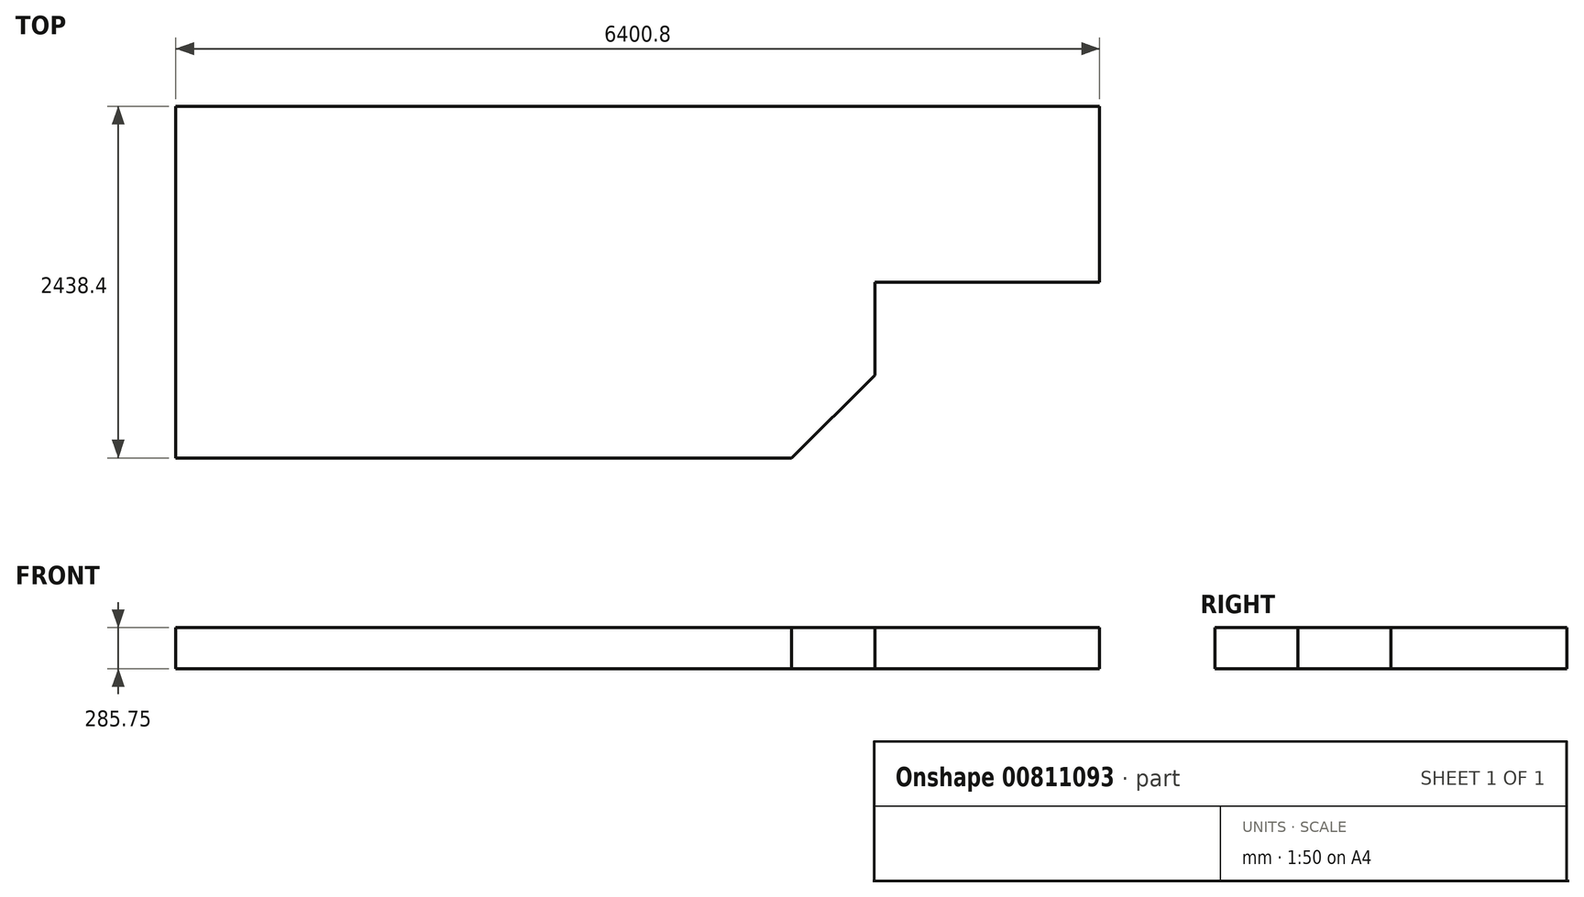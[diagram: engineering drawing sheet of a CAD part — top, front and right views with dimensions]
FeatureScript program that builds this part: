
annotation { "Feature Type Name" : "Feature", "Feature Type Description" : "" }
export const myFeature = defineFeature(function(context is Context, id is Id, definition is map)
    precondition{}
    {
        {
            var Q0;
            Q0=qCreatedBy(makeId("Top.planeOp"),FACE);
            var sketch = newSketch(context, id + "F0", { "sketchPlane" : qUnion([Q0])});
            skLineSegment(sketch, "E0", {"start": v(0, -2438.4) * mm, "end": v(1625.6, -2438.4) * mm});
            skLineSegment(sketch, "E1", {"start": v(4267.2, -2438.4) * mm, "end": v(4841.94, -1863.66) * mm});
            skLineSegment(sketch, "E2", {"start": v(4841.94, -1863.66) * mm, "end": v(4841.94, -1219.2) * mm});
            skLineSegment(sketch, "E3", {"start": v(4841.94, -1219.2) * mm, "end": v(5181.6, -1219.2) * mm});
            skLineSegment(sketch, "E4", {"start": v(5181.6, -1219.2) * mm, "end": v(6400.8, -1219.2) * mm});
            skLineSegment(sketch, "E5", {"start": v(6400.8, -1219.2) * mm, "end": v(6400.8, 0) * mm});
            skLineSegment(sketch, "E6", {"start": v(6400.8, 0) * mm, "end": v(0, 0) * mm});
            skLineSegment(sketch, "E7", {"start": v(1625.6, -2438.4) * mm, "end": v(3251.2, -2438.4) * mm});
            skLineSegment(sketch, "E8", {"start": v(3251.2, -2438.4) * mm, "end": v(4267.2, -2438.4) * mm});
            skLineSegment(sketch, "E9", {"start": v(0, 0) * mm, "end": v(0, -812.8) * mm});
            skLineSegment(sketch, "E10", {"start": v(0, -812.8) * mm, "end": v(0, -2438.4) * mm});
            skSolve(sketch);
        }
        {
            var Q0;
            Q0=makeQuery(id+"F0.imprint","IMPRINT",FACE,{"disambiguationData":[TD([[makeQuery(id+"F0.imprint","IMPRINT",EDGE,{"derivedFrom":sQuery(id+"F0.wireOp",EDGE,"E0")}),1.0]])]});
            extrude(context, id + "F1", {"entities" : qUnion([Q0]), "oppositeDirection" : true, "depth" : 285.75 * mm, "offsetDistance" : 25.4 * mm});
        }
    });
